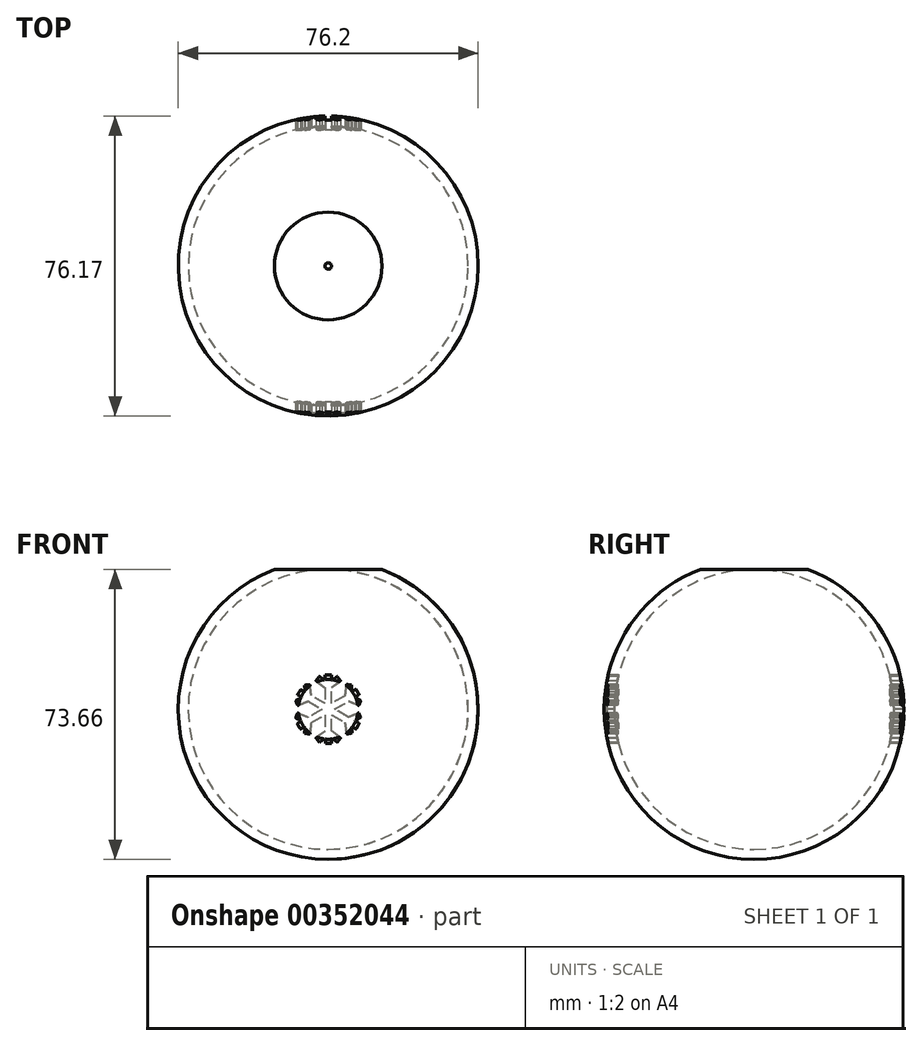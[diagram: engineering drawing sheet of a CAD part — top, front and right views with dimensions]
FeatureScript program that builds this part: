
annotation { "Feature Type Name" : "Feature", "Feature Type Description" : "" }
export const myFeature = defineFeature(function(context is Context, id is Id, definition is map)
    precondition{}
    {
        {
            var Q0;
            Q0=qCreatedBy(makeId("Front.planeOp"),FACE);
            var sketch = newSketch(context, id + "F0", { "sketchPlane" : qUnion([Q0])});
            skPoint(sketch, "E0.first.point", {"position": v(0, 0) * mm});
            skArc(sketch, "E1", {"start": v(0, -38.1) * mm, "mid": v(38.1, 0) * mm, "end": v(0, 38.1) * mm});
            skLineSegment(sketch, "E2", {"start": v(0, 38.1) * mm, "end": v(0, -38.1) * mm});
            skSolve(sketch);
        }
        {
            var Q0;
            Q0=makeQuery(id+"F0.imprint","IMPRINT",FACE,{"disambiguationData":[TD([[makeQuery(id+"F0.imprint","IMPRINT",EDGE,{"derivedFrom":sQuery(id+"F0.wireOp",EDGE,"E1")}),1.0]])]});
            var Q1;
            Q1=sQuery(id+"F0.wireOp",EDGE,"E2");
            revolve(context, id + "F1", {"entities" : qUnion([Q0]), "axis" : qUnion([Q1]), "revolveType" : RevolveType.FULL});
        }
        {
            var Q0;
            Q0=qCreatedBy(makeId("Top.planeOp"),FACE);
            cPlane(context, id + "F2", {"entities" : qUnion([Q0]), "cplaneType" : CPlaneType.OFFSET, "offset" : 35.56 * mm, "width" : 152.4 * mm, "height" : 152.4 * mm});
        }
        {
            var Q0;
            Q0=qCreatedBy(id+"F2.planeOp",FACE);
            var sketch = newSketch(context, id + "F3", { "sketchPlane" : qUnion([Q0])});
            skLineSegment(sketch, "E3.bottom", {"start": v(16.51, 16.51) * mm, "end": v(-16.51, 16.51) * mm});
            skLineSegment(sketch, "E3.top", {"start": v(16.51, -16.51) * mm, "end": v(-16.51, -16.51) * mm});
            skLineSegment(sketch, "E3.left", {"start": v(16.51, 16.51) * mm, "end": v(16.51, -16.51) * mm});
            skLineSegment(sketch, "E3.right", {"start": v(-16.51, 16.51) * mm, "end": v(-16.51, -16.51) * mm});
            skPoint(sketch, "E3.middle", {"position": v(0, 0) * mm});
            skSolve(sketch);
        }
        {
            var Q0;
            Q0=makeQuery(id+"F3.imprint","IMPRINT",FACE,{"disambiguationData":[TD([[makeQuery(id+"F3.imprint","IMPRINT",EDGE,{"derivedFrom":sQuery(id+"F3.wireOp",EDGE,"E3.bottom")}),1.0]])]});
            extrude(context, id + "F4", {"entities" : qUnion([Q0]), "operationType" : NewBodyOperationType.REMOVE, "depth" : 25.4 * mm});
        }
        {
            var Q0;
            Q0=makeQuery(id+"F4.boolean.opBoolean","COPY",FACE,{"derivedFrom":makeQuery(id+"F4.opExtrude","CAP_FACE",FACE,{"disambiguationData":[OSD([sQuery(id+"F3.wireOp",EDGE,"E3.bottom"),sQuery(id+"F3.wireOp",EDGE,"E3.top"),sQuery(id+"F3.wireOp",EDGE,"E3.left"),sQuery(id+"F3.wireOp",EDGE,"E3.right")])],"isStart":true})});
            shell(context, id + "F5", {"entities" : qUnion([Q0]), "thickness" : 2.54 * mm});
        }
        {
            var Q0;
            Q0=qCreatedBy(makeId("Front.planeOp"),FACE);
            cPlane(context, id + "F6", {"entities" : qUnion([Q0]), "cplaneType" : CPlaneType.OFFSET, "offset" : 37.34 * mm, "width" : 152.4 * mm, "height" : 152.4 * mm});
        }
        {
            var Q0;
            Q0=makeQuery(id+"FBe4SXbIVkiStFI_1.imprint","IMPRINT",FACE,{"disambiguationData":[TD([[makeQuery(id+"FBe4SXbIVkiStFI_1.imprint","IMPRINT",EDGE,{"derivedFrom":sQuery(id+"FBe4SXbIVkiStFI_1.wireOp",EDGE,"PHCpsiVz-8vEb-YAKC-MBQR-f1YV7AhH4J3M.bottom")}),-1.0]])]});
            var sketch = newSketch(context, id + "F7", { "sketchPlane" : qUnion([Q0])});
            skLineSegment(sketch, "E4", {"start": v(-0.77, 1.53) * mm, "end": v(-0.77, 5.48) * mm});
            skLineSegment(sketch, "E5", {"start": v(-0.77, 5.48) * mm, "end": v(-3.12, 7.26) * mm});
            skLineSegment(sketch, "E6", {"start": v(-3.12, 7.26) * mm, "end": v(-2.26, 8.4) * mm});
            skLineSegment(sketch, "E7", {"start": v(-2.26, 8.4) * mm, "end": v(-0.77, 7.26) * mm});
            skLineSegment(sketch, "E8", {"start": v(-0.77, 7.26) * mm, "end": v(-0.77, 8.72) * mm});
            skLineSegment(sketch, "E9", {"start": v(-0.77, 8.72) * mm, "end": v(0.83, 8.72) * mm});
            skLineSegment(sketch, "E10", {"start": v(0.83, 8.72) * mm, "end": v(0.83, 7.28) * mm});
            skLineSegment(sketch, "E11", {"start": v(0.83, 7.28) * mm, "end": v(2.3, 8.36) * mm});
            skLineSegment(sketch, "E12", {"start": v(2.3, 8.36) * mm, "end": v(3.1, 7.26) * mm});
            skLineSegment(sketch, "E13", {"start": v(3.1, 7.26) * mm, "end": v(0.83, 5.58) * mm});
            skLineSegment(sketch, "E14", {"start": v(0.83, 5.58) * mm, "end": v(0.83, 1.56) * mm});
            skLineSegment(sketch, "E15", {"start": v(0.83, 1.56) * mm, "end": v(4.27, 3.45) * mm});
            skLineSegment(sketch, "E16", {"start": v(4.27, 3.45) * mm, "end": v(4.61, 6.34) * mm});
            skLineSegment(sketch, "E17", {"start": v(4.61, 6.34) * mm, "end": v(5.9, 6.18) * mm});
            skLineSegment(sketch, "E18", {"start": v(5.9, 6.18) * mm, "end": v(5.82, 4.42) * mm});
            skLineSegment(sketch, "E19", {"start": v(5.82, 4.42) * mm, "end": v(7.05, 5.14) * mm});
            skLineSegment(sketch, "E20", {"start": v(7.05, 5.14) * mm, "end": v(7.83, 3.76) * mm});
            skLineSegment(sketch, "E21", {"start": v(7.83, 3.76) * mm, "end": v(6.69, 3.02) * mm});
            skLineSegment(sketch, "E22", {"start": v(6.69, 3.02) * mm, "end": v(8.27, 2.24) * mm});
            skLineSegment(sketch, "E23", {"start": v(8.27, 2.24) * mm, "end": v(7.8, 1) * mm});
            skLineSegment(sketch, "E24", {"start": v(7.8, 1) * mm, "end": v(5.18, 2.05) * mm});
            skLineSegment(sketch, "E25", {"start": v(5.18, 2.05) * mm, "end": v(1.65, 0.07) * mm});
            skLineSegment(sketch, "E26", {"start": v(1.65, 0.07) * mm, "end": v(5.08, -1.96) * mm});
            skLineSegment(sketch, "E27", {"start": v(5.08, -1.96) * mm, "end": v(7.75, -0.9) * mm});
            skLineSegment(sketch, "E28", {"start": v(7.75, -0.9) * mm, "end": v(8.22, -2.07) * mm});
            skLineSegment(sketch, "E29", {"start": v(8.22, -2.07) * mm, "end": v(6.7, -2.85) * mm});
            skLineSegment(sketch, "E30", {"start": v(6.7, -2.85) * mm, "end": v(7.87, -3.52) * mm});
            skLineSegment(sketch, "E31", {"start": v(7.87, -3.52) * mm, "end": v(7.1, -5) * mm});
            skLineSegment(sketch, "E32", {"start": v(7.1, -5) * mm, "end": v(5.88, -4.31) * mm});
            skLineSegment(sketch, "E33", {"start": v(5.88, -4.31) * mm, "end": v(6.05, -6) * mm});
            skLineSegment(sketch, "E34", {"start": v(6.05, -6) * mm, "end": v(4.7, -6.25) * mm});
            skLineSegment(sketch, "E35", {"start": v(4.7, -6.25) * mm, "end": v(4.28, -3.35) * mm});
            skLineSegment(sketch, "E36", {"start": v(4.28, -3.35) * mm, "end": v(0.87, -1.41) * mm});
            skLineSegment(sketch, "E37", {"start": v(0.87, -1.41) * mm, "end": v(0.87, -5.47) * mm});
            skLineSegment(sketch, "E38", {"start": v(0.87, -5.47) * mm, "end": v(3.13, -7.26) * mm});
            skLineSegment(sketch, "E39", {"start": v(3.13, -7.26) * mm, "end": v(2.28, -8.34) * mm});
            skLineSegment(sketch, "E40", {"start": v(2.28, -8.34) * mm, "end": v(0.87, -7.26) * mm});
            skLineSegment(sketch, "E41", {"start": v(0.87, -7.26) * mm, "end": v(0.87, -8.67) * mm});
            skLineSegment(sketch, "E42", {"start": v(0.87, -8.67) * mm, "end": v(-0.74, -8.67) * mm});
            skLineSegment(sketch, "E43", {"start": v(-0.74, -8.67) * mm, "end": v(-0.74, -7.32) * mm});
            skLineSegment(sketch, "E44", {"start": v(-0.74, -7.32) * mm, "end": v(-2.21, -8.4) * mm});
            skLineSegment(sketch, "E45", {"start": v(-2.21, -8.4) * mm, "end": v(-3.12, -7.26) * mm});
            skLineSegment(sketch, "E46", {"start": v(-3.12, -7.26) * mm, "end": v(-0.82, -5.57) * mm});
            skLineSegment(sketch, "E47", {"start": v(-0.82, -5.57) * mm, "end": v(-0.82, -1.41) * mm});
            skLineSegment(sketch, "E48", {"start": v(-0.82, -1.41) * mm, "end": v(-4.28, -3.35) * mm});
            skLineSegment(sketch, "E49", {"start": v(-4.28, -3.35) * mm, "end": v(-4.62, -6.25) * mm});
            skLineSegment(sketch, "E50", {"start": v(-4.62, -6.25) * mm, "end": v(-6.03, -6.09) * mm});
            skLineSegment(sketch, "E51", {"start": v(-6.03, -6.09) * mm, "end": v(-5.82, -4.3) * mm});
            skLineSegment(sketch, "E52", {"start": v(-5.82, -4.3) * mm, "end": v(-7.09, -5) * mm});
            skLineSegment(sketch, "E53", {"start": v(-7.09, -5) * mm, "end": v(-7.88, -3.61) * mm});
            skLineSegment(sketch, "E54", {"start": v(-7.88, -3.61) * mm, "end": v(-6.67, -2.93) * mm});
            skLineSegment(sketch, "E55", {"start": v(-6.67, -2.93) * mm, "end": v(-8.27, -2.16) * mm});
            skLineSegment(sketch, "E56", {"start": v(-8.27, -2.16) * mm, "end": v(-7.77, -0.92) * mm});
            skLineSegment(sketch, "E57", {"start": v(-7.77, -0.92) * mm, "end": v(-5.08, -2.01) * mm});
            skLineSegment(sketch, "E58", {"start": v(-5.08, -2.01) * mm, "end": v(-1.59, 0) * mm});
            skLineSegment(sketch, "E59", {"start": v(-1.59, 0) * mm, "end": v(-5.06, 2.06) * mm});
            skLineSegment(sketch, "E60", {"start": v(-5.06, 2.06) * mm, "end": v(-7.74, 0.97) * mm});
            skLineSegment(sketch, "E61", {"start": v(-7.74, 0.97) * mm, "end": v(-8.25, 2.24) * mm});
            skLineSegment(sketch, "E62", {"start": v(-8.25, 2.24) * mm, "end": v(-6.6, 3) * mm});
            skLineSegment(sketch, "E63", {"start": v(-6.6, 3) * mm, "end": v(-7.8, 3.72) * mm});
            skLineSegment(sketch, "E64", {"start": v(-7.8, 3.72) * mm, "end": v(-7.01, 5.01) * mm});
            skLineSegment(sketch, "E65", {"start": v(-7.01, 5.01) * mm, "end": v(-5.83, 4.4) * mm});
            skLineSegment(sketch, "E66", {"start": v(-5.83, 4.4) * mm, "end": v(-6.01, 6.13) * mm});
            skLineSegment(sketch, "E67", {"start": v(-6.01, 6.13) * mm, "end": v(-4.67, 6.27) * mm});
            skLineSegment(sketch, "E68", {"start": v(-4.67, 6.27) * mm, "end": v(-4.37, 3.5) * mm});
            skLineSegment(sketch, "E69", {"start": v(-4.37, 3.5) * mm, "end": v(-0.77, 1.53) * mm});
            skSolve(sketch);
        }
        {
            var Q0;
            Q0=qCreatedBy(id+"F6.planeOp",FACE);
            var sketch = newSketch(context, id + "F8", { "sketchPlane" : qUnion([Q0])});
            skLineSegment(sketch, "E70.0.0", {"start": v(-0.77, 1.53) * mm, "end": v(-4.37, 3.5) * mm});
            skLineSegment(sketch, "E70.0.1", {"start": v(-4.37, 3.5) * mm, "end": v(-4.67, 6.27) * mm});
            skLineSegment(sketch, "E70.0.2", {"start": v(-4.67, 6.27) * mm, "end": v(-6.01, 6.13) * mm});
            skLineSegment(sketch, "E70.0.3", {"start": v(-6.01, 6.13) * mm, "end": v(-5.83, 4.4) * mm});
            skLineSegment(sketch, "E70.0.4", {"start": v(-5.83, 4.4) * mm, "end": v(-7.01, 5.01) * mm});
            skLineSegment(sketch, "E70.0.5", {"start": v(-7.01, 5.01) * mm, "end": v(-7.8, 3.72) * mm});
            skLineSegment(sketch, "E70.0.6", {"start": v(-7.8, 3.72) * mm, "end": v(-6.6, 3) * mm});
            skLineSegment(sketch, "E70.0.7", {"start": v(-6.6, 3) * mm, "end": v(-8.25, 2.24) * mm});
            skLineSegment(sketch, "E70.0.8", {"start": v(-8.25, 2.24) * mm, "end": v(-7.74, 0.97) * mm});
            skLineSegment(sketch, "E70.0.9", {"start": v(-7.74, 0.97) * mm, "end": v(-5.06, 2.06) * mm});
            skLineSegment(sketch, "E70.0.10", {"start": v(-5.06, 2.06) * mm, "end": v(-1.59, 0) * mm});
            skLineSegment(sketch, "E70.0.11", {"start": v(-1.59, 0) * mm, "end": v(-5.08, -2.01) * mm});
            skLineSegment(sketch, "E70.0.12", {"start": v(-5.08, -2.01) * mm, "end": v(-7.77, -0.92) * mm});
            skLineSegment(sketch, "E70.0.13", {"start": v(-7.77, -0.92) * mm, "end": v(-8.27, -2.16) * mm});
            skLineSegment(sketch, "E70.0.14", {"start": v(-8.27, -2.16) * mm, "end": v(-6.67, -2.93) * mm});
            skLineSegment(sketch, "E70.0.15", {"start": v(-6.67, -2.93) * mm, "end": v(-7.88, -3.61) * mm});
            skLineSegment(sketch, "E70.0.16", {"start": v(-7.88, -3.61) * mm, "end": v(-7.09, -5) * mm});
            skLineSegment(sketch, "E70.0.17", {"start": v(-7.09, -5) * mm, "end": v(-5.82, -4.3) * mm});
            skLineSegment(sketch, "E70.0.18", {"start": v(-5.82, -4.3) * mm, "end": v(-6.03, -6.09) * mm});
            skLineSegment(sketch, "E70.0.19", {"start": v(-6.03, -6.09) * mm, "end": v(-4.62, -6.25) * mm});
            skLineSegment(sketch, "E70.0.20", {"start": v(-4.62, -6.25) * mm, "end": v(-4.28, -3.35) * mm});
            skLineSegment(sketch, "E70.0.21", {"start": v(-4.28, -3.35) * mm, "end": v(-0.82, -1.41) * mm});
            skLineSegment(sketch, "E70.0.22", {"start": v(-0.82, -1.41) * mm, "end": v(-0.82, -5.57) * mm});
            skLineSegment(sketch, "E70.0.23", {"start": v(-0.82, -5.57) * mm, "end": v(-3.12, -7.26) * mm});
            skLineSegment(sketch, "E70.0.24", {"start": v(-3.12, -7.26) * mm, "end": v(-2.21, -8.4) * mm});
            skLineSegment(sketch, "E70.0.25", {"start": v(-2.21, -8.4) * mm, "end": v(-0.74, -7.32) * mm});
            skLineSegment(sketch, "E70.0.26", {"start": v(-0.74, -7.32) * mm, "end": v(-0.74, -8.67) * mm});
            skLineSegment(sketch, "E70.0.27", {"start": v(-0.74, -8.67) * mm, "end": v(0.87, -8.67) * mm});
            skLineSegment(sketch, "E70.0.28", {"start": v(0.87, -8.67) * mm, "end": v(0.87, -7.26) * mm});
            skLineSegment(sketch, "E70.0.29", {"start": v(0.87, -7.26) * mm, "end": v(2.28, -8.34) * mm});
            skLineSegment(sketch, "E70.0.30", {"start": v(2.28, -8.34) * mm, "end": v(3.13, -7.26) * mm});
            skLineSegment(sketch, "E70.0.31", {"start": v(3.13, -7.26) * mm, "end": v(0.87, -5.47) * mm});
            skLineSegment(sketch, "E70.0.32", {"start": v(0.87, -5.47) * mm, "end": v(0.87, -1.41) * mm});
            skLineSegment(sketch, "E70.0.33", {"start": v(0.87, -1.41) * mm, "end": v(4.28, -3.35) * mm});
            skLineSegment(sketch, "E70.0.34", {"start": v(4.28, -3.35) * mm, "end": v(4.7, -6.25) * mm});
            skLineSegment(sketch, "E70.0.35", {"start": v(4.7, -6.25) * mm, "end": v(6.05, -6) * mm});
            skLineSegment(sketch, "E70.0.36", {"start": v(6.05, -6) * mm, "end": v(5.88, -4.31) * mm});
            skLineSegment(sketch, "E70.0.37", {"start": v(5.88, -4.31) * mm, "end": v(7.1, -5) * mm});
            skLineSegment(sketch, "E70.0.38", {"start": v(7.1, -5) * mm, "end": v(7.87, -3.52) * mm});
            skLineSegment(sketch, "E70.0.39", {"start": v(7.87, -3.52) * mm, "end": v(6.7, -2.85) * mm});
            skLineSegment(sketch, "E70.0.40", {"start": v(6.7, -2.85) * mm, "end": v(8.22, -2.07) * mm});
            skLineSegment(sketch, "E70.0.41", {"start": v(8.22, -2.07) * mm, "end": v(7.75, -0.9) * mm});
            skLineSegment(sketch, "E70.0.42", {"start": v(7.75, -0.9) * mm, "end": v(5.08, -1.96) * mm});
            skLineSegment(sketch, "E70.0.43", {"start": v(5.08, -1.96) * mm, "end": v(1.65, 0.07) * mm});
            skLineSegment(sketch, "E70.0.44", {"start": v(1.65, 0.07) * mm, "end": v(5.18, 2.05) * mm});
            skLineSegment(sketch, "E70.0.45", {"start": v(5.18, 2.05) * mm, "end": v(7.8, 1) * mm});
            skLineSegment(sketch, "E70.0.46", {"start": v(7.8, 1) * mm, "end": v(8.27, 2.24) * mm});
            skLineSegment(sketch, "E70.0.47", {"start": v(8.27, 2.24) * mm, "end": v(6.69, 3.02) * mm});
            skLineSegment(sketch, "E70.0.48", {"start": v(6.69, 3.02) * mm, "end": v(7.83, 3.76) * mm});
            skLineSegment(sketch, "E70.0.49", {"start": v(7.83, 3.76) * mm, "end": v(7.05, 5.14) * mm});
            skLineSegment(sketch, "E70.0.50", {"start": v(7.05, 5.14) * mm, "end": v(5.82, 4.42) * mm});
            skLineSegment(sketch, "E70.0.51", {"start": v(5.82, 4.42) * mm, "end": v(5.9, 6.18) * mm});
            skLineSegment(sketch, "E70.0.52", {"start": v(5.9, 6.18) * mm, "end": v(4.61, 6.34) * mm});
            skLineSegment(sketch, "E70.0.53", {"start": v(4.61, 6.34) * mm, "end": v(4.27, 3.45) * mm});
            skLineSegment(sketch, "E70.0.54", {"start": v(4.27, 3.45) * mm, "end": v(0.83, 1.56) * mm});
            skLineSegment(sketch, "E70.0.55", {"start": v(0.83, 1.56) * mm, "end": v(0.83, 5.58) * mm});
            skLineSegment(sketch, "E70.0.56", {"start": v(0.83, 5.58) * mm, "end": v(3.1, 7.26) * mm});
            skLineSegment(sketch, "E70.0.57", {"start": v(3.1, 7.26) * mm, "end": v(2.3, 8.36) * mm});
            skLineSegment(sketch, "E70.0.58", {"start": v(2.3, 8.36) * mm, "end": v(0.83, 7.28) * mm});
            skLineSegment(sketch, "E70.0.59", {"start": v(0.83, 7.28) * mm, "end": v(0.83, 8.72) * mm});
            skLineSegment(sketch, "E70.0.60", {"start": v(0.83, 8.72) * mm, "end": v(-0.77, 8.72) * mm});
            skLineSegment(sketch, "E70.0.61", {"start": v(-0.77, 8.72) * mm, "end": v(-0.77, 7.26) * mm});
            skLineSegment(sketch, "E70.0.62", {"start": v(-0.77, 7.26) * mm, "end": v(-2.26, 8.4) * mm});
            skLineSegment(sketch, "E70.0.63", {"start": v(-2.26, 8.4) * mm, "end": v(-3.12, 7.26) * mm});
            skLineSegment(sketch, "E70.0.64", {"start": v(-3.12, 7.26) * mm, "end": v(-0.77, 5.48) * mm});
            skLineSegment(sketch, "E70.0.65", {"start": v(-0.77, 5.48) * mm, "end": v(-0.77, 1.53) * mm});
            skSolve(sketch);
        }
        {
            var Q0;
            Q0 = qSketchRegion(id + "F8", true);
            extrude(context, id + "F9", {"entities" : qUnion([Q0]), "operationType" : NewBodyOperationType.REMOVE, "oppositeDirection" : true, "depth" : 81.28 * mm});
        }
    });
